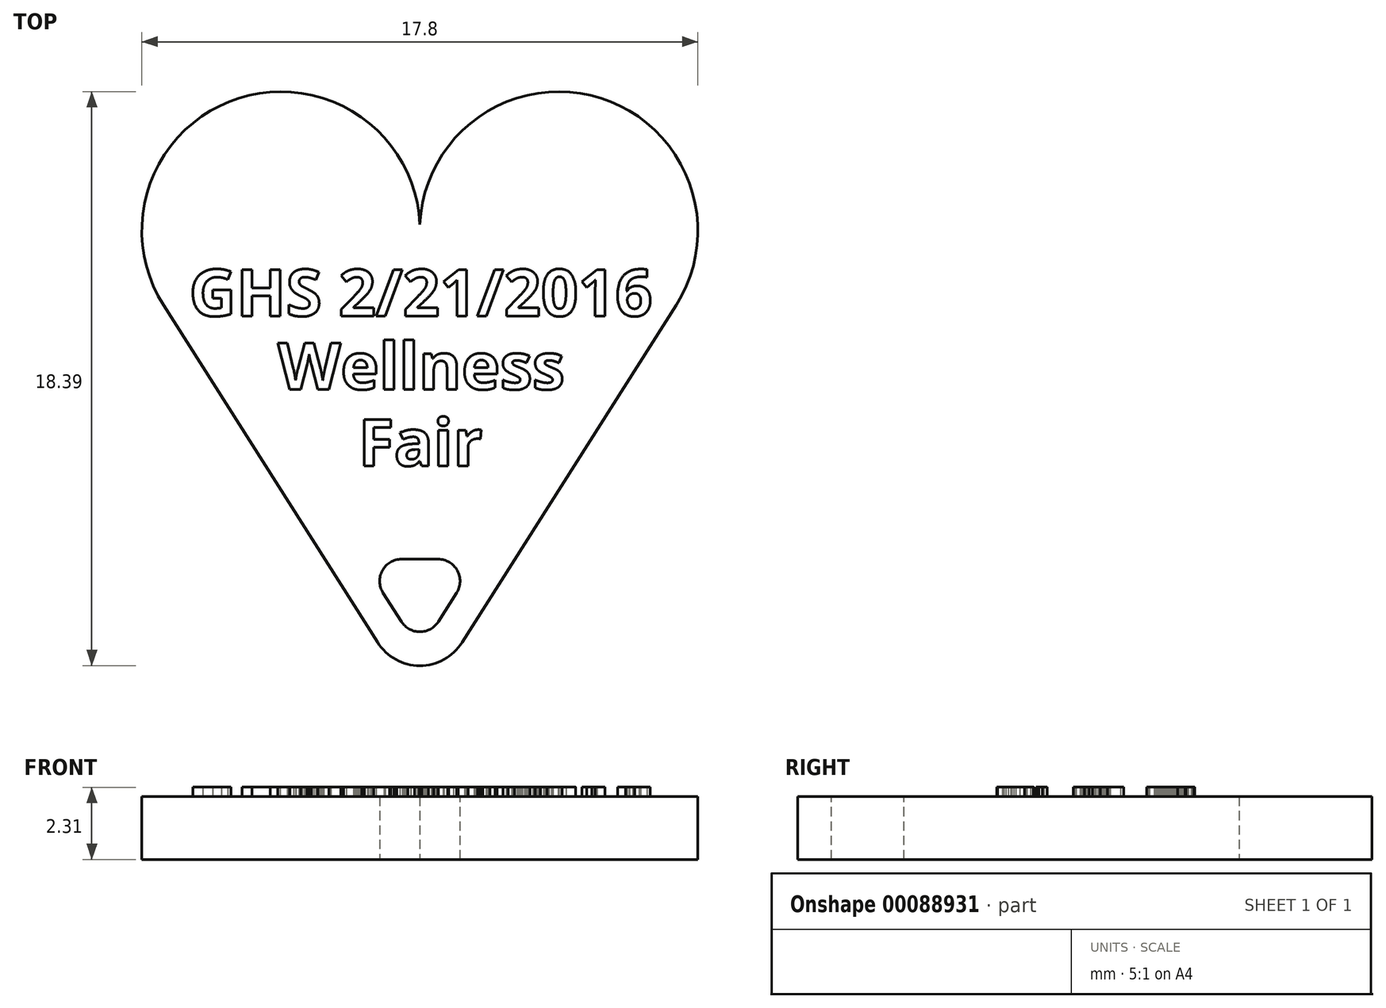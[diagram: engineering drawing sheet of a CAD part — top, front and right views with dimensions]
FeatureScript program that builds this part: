
annotation { "Feature Type Name" : "Feature", "Feature Type Description" : "" }
export const myFeature = defineFeature(function(context is Context, id is Id, definition is map)
    precondition{}
    {
        {
            var Q0;
            Q0=qCreatedBy(makeId("Top.planeOp"),FACE);
            var sketch = newSketch(context, id + "F0", { "sketchPlane" : qUnion([Q0])});
            skArc(sketch, "E0", {"start": v(0, 4.6) * mm, "mid": v(-5.6, 9.1) * mm, "end": v(-8.2, 2.4) * mm});
            skPoint(sketch, "E0.first.point", {"position": v(0, 5) * mm});
            skPoint(sketch, "E0.second.point", {"position": v(-4.82, 9.23) * mm});
            skPoint(sketch, "E0.third.point", {"position": v(-7.74, 1.8) * mm});
            skLineSegment(sketch, "E1", {"start": v(0, -17.44) * mm, "end": v(0, 15.54) * mm, "construction": true});
            skArc(sketch, "E2.MirrorC", {"start": v(0, 4.6) * mm, "mid": v(5.6, 9.1) * mm, "end": v(8.2, 2.4) * mm});
            skLineSegment(sketch, "E3", {"start": v(-8.2, 2.4) * mm, "end": v(0, -10.53) * mm});
            skLineSegment(sketch, "E4.MirrorCS", {"start": v(8.2, 2.4) * mm, "end": v(0, -10.53) * mm});
            skSolve(sketch);
        }
        {
            var Q0;
            Q0 = qSketchRegion(id + "F0", true);
            extrude(context, id + "F1", {"entities" : qUnion([Q0]), "depth" : 2 * mm});
        }
        {
            var Q0;
            Q0=makeQuery(id+"F1.opExtrude","CAP_FACE",FACE,{"disambiguationData":[OSD([sQuery(id+"F0.wireOp",EDGE,"E0"),sQuery(id+"F0.wireOp",EDGE,"E2.MirrorC"),sQuery(id+"F0.wireOp",EDGE,"E3"),sQuery(id+"F0.wireOp",EDGE,"E4.MirrorCS")])],"isStart":false});
            var sketch = newSketch(context, id + "F2", { "sketchPlane" : qUnion([Q0])});
            skLineSegment(sketch, "E5.0", {"start": v(0, -8.66) * mm, "end": v(1.86, -5.73) * mm});
            skLineSegment(sketch, "E6", {"start": v(-1.86, -5.73) * mm, "end": v(1.86, -5.73) * mm});
            skPoint(sketch, "E7.orphan", {"position": v(2.7, -6.27) * mm});
            skLineSegment(sketch, "E8.trimOffspring", {"start": v(0, -8.66) * mm, "end": v(-1.86, -5.73) * mm});
            skPoint(sketch, "E9.end.orphan", {"position": v(-2.7, -6.27) * mm});
            skSolve(sketch);
        }
        {
            var Q0;
            Q0=makeQuery(id+"F2.imprint","IMPRINT",FACE,{"disambiguationData":[TD([[makeQuery(id+"F2.imprint","IMPRINT",EDGE,{"derivedFrom":sQuery(id+"F2.wireOp",EDGE,"E5.0")}),1.0]])]});
            var Q1;
            Q1=makeQuery(id+"F1.opExtrude","CAP_FACE",FACE,{"disambiguationData":[OSD([sQuery(id+"F0.wireOp",EDGE,"E0"),sQuery(id+"F0.wireOp",EDGE,"E2.MirrorC"),sQuery(id+"F0.wireOp",EDGE,"E3"),sQuery(id+"F0.wireOp",EDGE,"E4.MirrorCS")])],"isStart":true});
            extrude(context, id + "F3", {"entities" : qUnion([Q0]), "operationType" : NewBodyOperationType.REMOVE, "endBound" : BoundingType.UP_TO_SURFACE, "oppositeDirection" : true, "endBoundEntityFace" : qUnion([Q1]), "depth" : 25 * mm});
        }
        {
            var Q0;
            Q0=makeQuery(id+"F3.boolean.opBoolean","COPY",EDGE,{"derivedFrom":makeQuery(id+"F3.opExtrude","SWEPT_EDGE",EDGE,{"disambiguationData":[OSD([sQuery(id+"F2.wireOp",EDGE,"E6"),sQuery(id+"F2.wireOp",EDGE,"E8.trimOffspring")])]})});
            var Q1;
            Q1=makeQuery(id+"F3.boolean.opBoolean","COPY",EDGE,{"derivedFrom":makeQuery(id+"F3.opExtrude","SWEPT_EDGE",EDGE,{"disambiguationData":[OSD([sQuery(id+"F2.wireOp",EDGE,"E5.0"),sQuery(id+"F2.wireOp",EDGE,"E6")])]})});
            var Q2;
            Q2=makeQuery(id+"F3.boolean.opBoolean","COPY",EDGE,{"derivedFrom":makeQuery(id+"F3.opExtrude","SWEPT_EDGE",EDGE,{"disambiguationData":[OSD([sQuery(id+"F2.wireOp",EDGE,"E5.0"),sQuery(id+"F2.wireOp",EDGE,"E8.trimOffspring")])]})});
            fillet(context, id + "F4", {"entities" : qUnion([Q0, Q1, Q2]), "radius" : 0.7 * mm, "tangentPropagation" : true, "allowEdgeOverflow" : false});
        }
        {
            var Q0;
            Q0=makeQuery(id+"F1.opExtrude","CAP_FACE",FACE,{"disambiguationData":[OSD([sQuery(id+"F0.wireOp",EDGE,"E0"),sQuery(id+"F0.wireOp",EDGE,"E2.MirrorC"),sQuery(id+"F0.wireOp",EDGE,"E3"),sQuery(id+"F0.wireOp",EDGE,"E4.MirrorCS")])],"isStart":false});
            var sketch = newSketch(context, id + "F5", { "sketchPlane" : qUnion([Q0])});
            skText(sketch, "E10", { "text": "GHS 2/21/2016", "fontName": "OpenSans-Bold.ttf"});
            skText(sketch, "E11", { "text": "Wellness", "fontName": "OpenSans-Bold.ttf"});
            skText(sketch, "E12", { "text": "Fair\n", "fontName": "OpenSans-Bold.ttf"});
            const initialGuessF5  = {"E10": [-0.00739, 0.00206, 1, 0, 0.0015], "E11": [-0.00455, -0.00029, 1, 0, 0.0015], "E12": [-0.00197, -0.00274, 1, 0, 0.0015]};
            skSetInitialGuess(sketch, initialGuessF5);
            skSolve(sketch);
        }
        {
            var Q0;
            Q0 = qSketchRegion(id + "F5", true);
            extrude(context, id + "F6", {"entities" : qUnion([Q0]), "operationType" : NewBodyOperationType.ADD, "depth" : 0.2 * mm});
        }
        {
            var Q0;
            Q0=makeQuery(id+"F1.opExtrude","SWEPT_EDGE",EDGE,{"disambiguationData":[OSD([sQuery(id+"F0.wireOp",EDGE,"E3"),sQuery(id+"F0.wireOp",EDGE,"E4.MirrorCS")])]});
            fillet(context, id + "F7", {"entities" : qUnion([Q0]), "radius" : 1.6 * mm, "tangentPropagation" : true, "allowEdgeOverflow" : false});
        }
        {
            var Q0;
            Q0 = qSketchRegion(id + "F5", true);
            extrude(context, id + "F8", {"entities" : qUnion([Q0]), "operationType" : NewBodyOperationType.ADD, "depth" : .3 * mm});
        }
    });
